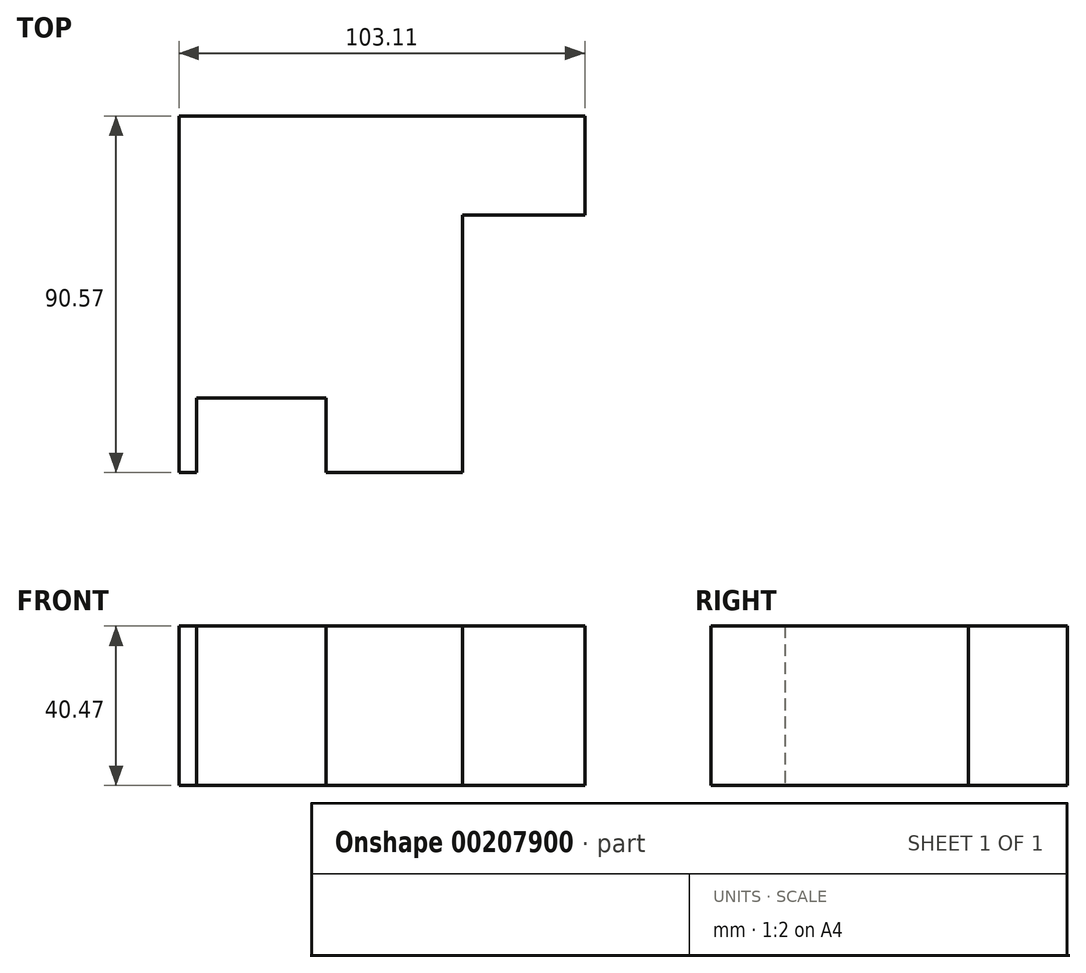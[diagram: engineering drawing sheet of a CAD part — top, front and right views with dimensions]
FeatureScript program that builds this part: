
annotation { "Feature Type Name" : "Feature", "Feature Type Description" : "" }
export const myFeature = defineFeature(function(context is Context, id is Id, definition is map)
    precondition{}
    {
        {
            var Q0;
            Q0=qCreatedBy(makeId("Top.planeOp"),FACE);
            var sketch = newSketch(context, id + "F0", { "sketchPlane" : qUnion([Q0])});
            skLineSegment(sketch, "E0.bottom", {"start": v(-52.59, 39.66) * mm, "end": v(50.52, 39.66) * mm});
            skLineSegment(sketch, "E0.top", {"start": v(-52.59, -50.91) * mm, "end": v(50.52, -50.91) * mm});
            skLineSegment(sketch, "E0.left", {"start": v(-52.59, 39.66) * mm, "end": v(-52.59, -50.91) * mm});
            skLineSegment(sketch, "E0.right", {"start": v(50.52, 39.66) * mm, "end": v(50.52, -50.91) * mm});
            skLineSegment(sketch, "E1.bottom", {"start": v(-48.08, -65.58) * mm, "end": v(-15.2, -65.58) * mm});
            skLineSegment(sketch, "E1.top", {"start": v(-48.08, -32.01) * mm, "end": v(-15.2, -32.01) * mm});
            skLineSegment(sketch, "E1.left", {"start": v(-48.08, -65.58) * mm, "end": v(-48.08, -32.01) * mm});
            skLineSegment(sketch, "E1.right", {"start": v(-15.2, -65.58) * mm, "end": v(-15.2, -32.01) * mm});
            skLineSegment(sketch, "E2.bottom", {"start": v(70.07, -70.94) * mm, "end": v(19.4, -70.94) * mm});
            skLineSegment(sketch, "E2.top", {"start": v(70.07, 14.5) * mm, "end": v(19.4, 14.5) * mm});
            skLineSegment(sketch, "E2.left", {"start": v(70.07, -70.94) * mm, "end": v(70.07, 14.5) * mm});
            skLineSegment(sketch, "E2.right", {"start": v(19.4, -70.94) * mm, "end": v(19.4, 14.5) * mm});
            skSolve(sketch);
        }
        {
            var Q0;
            {var subQ10=sQuery(id+"F0.wireOp",EDGE,"E0.bottom");Q0=makeQuery(id+"F0.imprint","IMPRINT",FACE,{"disambiguationData":[TD([[makeQuery(id+"F0.imprint","IMPRINT",EDGE,{"derivedFrom":subQ10}),-1.0]])]});}
            extrude(context, id + "F1", {"entities" : qUnion([Q0]), "depth" : 40.47 * mm});
        }
    });
